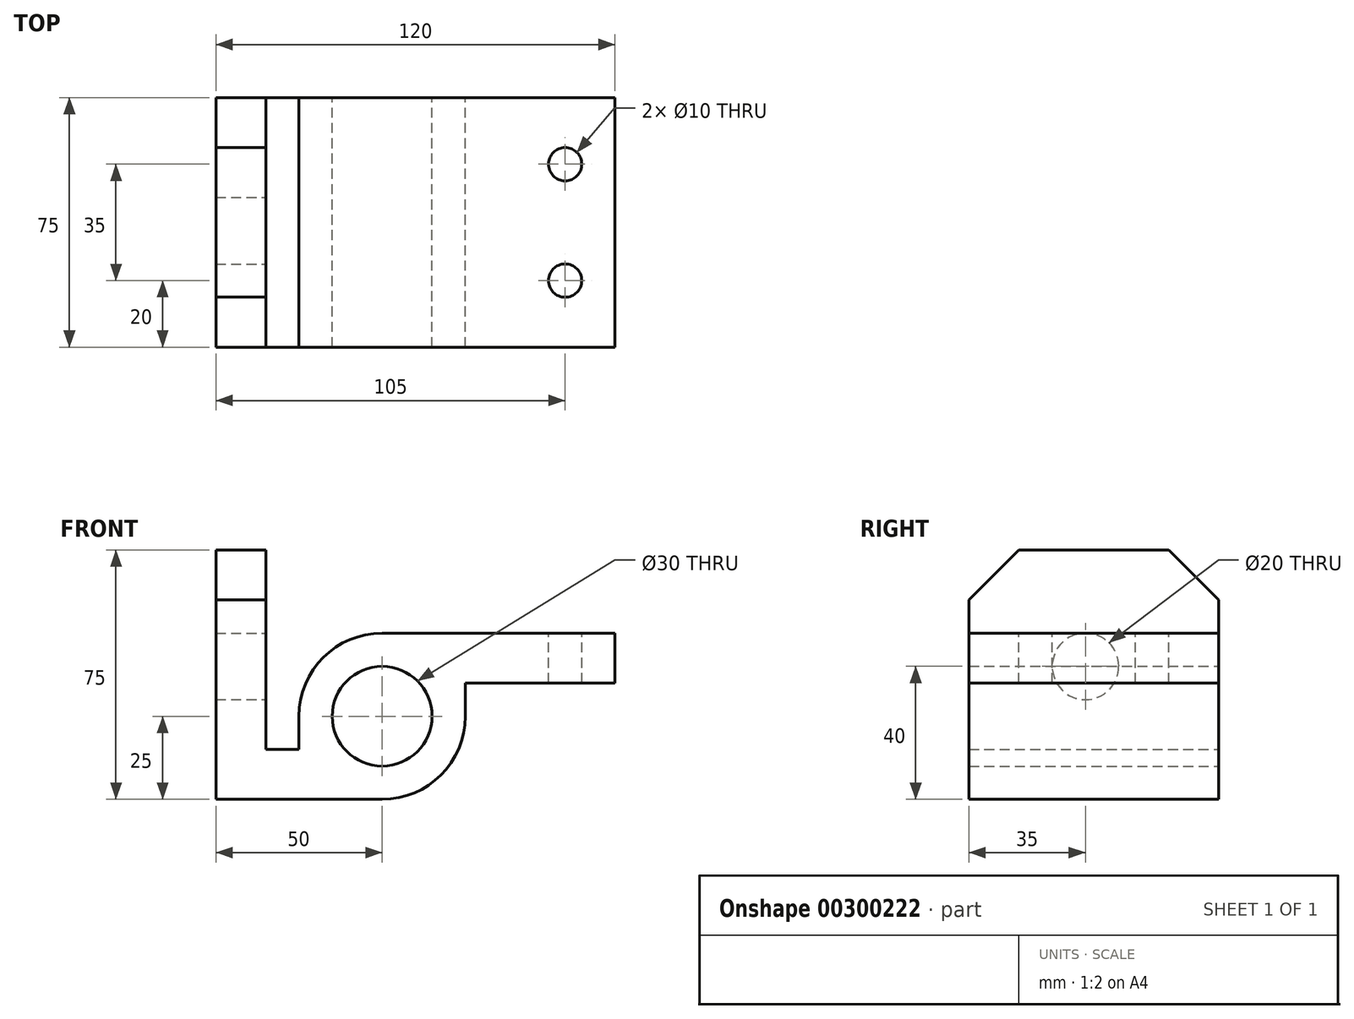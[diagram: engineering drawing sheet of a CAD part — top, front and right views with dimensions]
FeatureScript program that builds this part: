
annotation { "Feature Type Name" : "Feature", "Feature Type Description" : "" }
export const myFeature = defineFeature(function(context is Context, id is Id, definition is map)
    precondition{}
    {
        {
            var Q0;
            Q0=qCreatedBy(makeId("Front.planeOp"),FACE);
            var sketch = newSketch(context, id + "F0", { "sketchPlane" : qUnion([Q0])});
            skLineSegment(sketch, "E0.bottom", {"start": v(0, -25) * mm, "end": v(-25, -25) * mm});
            skLineSegment(sketch, "E0.top", {"start": v(25, 25) * mm, "end": v(0, 25) * mm});
            skLineSegment(sketch, "E0.left", {"start": v(25, 0) * mm, "end": v(25, 25) * mm});
            skLineSegment(sketch, "E0.right", {"start": v(-25, -25) * mm, "end": v(-25, 0) * mm});
            skPoint(sketch, "E0.middle", {"position": v(0, 0) * mm});
            skLineSegment(sketch, "E1", {"start": v(-25, -25) * mm, "end": v(-50, -25) * mm});
            skLineSegment(sketch, "E2", {"start": v(-25, -10) * mm, "end": v(-35, -10) * mm});
            skLineSegment(sketch, "E3", {"start": v(-35, -10) * mm, "end": v(-35, 50) * mm});
            skLineSegment(sketch, "E4", {"start": v(-35, 50) * mm, "end": v(-50, 50) * mm});
            skLineSegment(sketch, "E5", {"start": v(-50, 50) * mm, "end": v(-50, -25) * mm});
            skLineSegment(sketch, "E6", {"start": v(-50, 35) * mm, "end": v(-35, 35) * mm});
            skLineSegment(sketch, "E7", {"start": v(25, 25) * mm, "end": v(70, 25) * mm});
            skLineSegment(sketch, "E8", {"start": v(70, 25) * mm, "end": v(70, 10) * mm});
            skLineSegment(sketch, "E9", {"start": v(70, 10) * mm, "end": v(25, 10) * mm});
            skCircle(sketch, "E10", {"center": v(0, 0) * mm, "radius": 15 * mm});
            skPoint(sketch, "E11.visualSharp", {"position": v(25, -25) * mm});
            skArc(sketch, "E11.filletArc", {"start": v(0, -25) * mm, "mid": v(17.68, -17.68) * mm, "end": v(25, 0) * mm});
            skPoint(sketch, "E12.visualSharp", {"position": v(-25, 25) * mm});
            skArc(sketch, "E12.filletArc", {"start": v(0, 25) * mm, "mid": v(-17.68, 17.68) * mm, "end": v(-25, 0) * mm});
            skSolve(sketch);
        }
        {
            var Q0;
            Q0 = qSketchRegion(id + "F0", true);
            extrude(context, id + "F1", {"entities" : qUnion([Q0]), "endBound" : BoundingType.SYMMETRIC, "depth" : 75 * mm});
        }
        {
            var Q0;
            Q0=makeQuery(id+"F1.opExtrude","CAP_EDGE",EDGE,{"disambiguationData":[OSD([sQuery(id+"F0.wireOp",EDGE,"E4")])],"isStart":false});
            var Q1;
            Q1=makeQuery(id+"F1.opExtrude","CAP_EDGE",EDGE,{"disambiguationData":[OSD([sQuery(id+"F0.wireOp",EDGE,"E4")])],"isStart":true});
            chamfer(context, id + "F2", {"entities" : qUnion([Q0, Q1]), "width" : 15 * mm, "tangentPropagation" : true});
        }
        {
            var Q0;
            Q0=makeQuery(id+"F1.opExtrude","SWEPT_FACE",FACE,{"disambiguationData":[OSD([sQuery(id+"F0.wireOp",EDGE,"E3")])]});
            var sketch = newSketch(context, id + "F3", { "sketchPlane" : qUnion([Q0])});
            skPoint(sketch, "E13.endSnap0", {"position": v(-37.5, 12.5) * mm});
            skCircle(sketch, "E14", {"center": v(-2.5, 15) * mm, "radius": 10 * mm});
            skLineSegment(sketch, "E15", {"start": v(-2.5, 15) * mm, "end": v(-37.5, 15) * mm});
            skLineSegment(sketch, "E16", {"start": v(-2.5, 15) * mm, "end": v(-2.5, 50) * mm});
            skSolve(sketch);
        }
        {
            var Q0;
            {var subQ0=sQuery(id+"F3.wireOp",EDGE,"E15");var subQ1=sQuery(id+"F3.wireOp",EDGE,"E14");var subQ2=makeQuery(id+"F3.imprint","INTERSECT",VERTEX,{"derivedFrom":[subQ1,subQ0]});Q0=makeQuery(id+"F3.imprint","IMPRINT",FACE,{"disambiguationData":[TD([[makeQuery(id+"F3.imprint","IMPRINT",EDGE,{"disambiguationData":[TD([[subQ2,-1.0]])],"derivedFrom":subQ1}),1.0]])]});}
            var Q1;
            Q1=sQuery(id+"F3.wireOp",EDGE,"E14");
            var Q2;
            Q2=makeQuery(id+"F1.opExtrude","SWEPT_FACE",FACE,{"disambiguationData":[OSD([sQuery(id+"F0.wireOp",EDGE,"E5")])]});
            extrude(context, id + "F4", {"entities" : qUnion([Q0]), "operationType" : NewBodyOperationType.ADD, "surfaceEntities" : qUnion([Q1]), "endBound" : BoundingType.UP_TO_SURFACE, "oppositeDirection" : true, "endBoundEntityFace" : qUnion([Q2]), "depth" : 25 * mm});
        }
        {
            var Q0;
            Q0=sQuery(id+"F3.wireOp",VERTEX,"E15.start");
            var Q1;
            Q1=makeQuery(id+"F1.opExtrude","SWEPT_BODY",BODY,{"disambiguationData":[OSD([sQuery(id+"F0.wireOp",EDGE,"E0.bottom"),sQuery(id+"F0.wireOp",EDGE,"E0.top"),sQuery(id+"F0.wireOp",EDGE,"E0.left"),sQuery(id+"F0.wireOp",EDGE,"E0.right"),sQuery(id+"F0.wireOp",EDGE,"E1"),sQuery(id+"F0.wireOp",EDGE,"E2"),sQuery(id+"F0.wireOp",EDGE,"E3"),sQuery(id+"F0.wireOp",EDGE,"E4"),sQuery(id+"F0.wireOp",EDGE,"E5"),sQuery(id+"F0.wireOp",EDGE,"E7"),sQuery(id+"F0.wireOp",EDGE,"E8"),sQuery(id+"F0.wireOp",EDGE,"E9"),sQuery(id+"F0.wireOp",EDGE,"E10"),sQuery(id+"F0.wireOp",EDGE,"E11.filletArc"),sQuery(id+"F0.wireOp",EDGE,"E12.filletArc")])]});
            hole(context, id + "F5", {"style" : HoleStyle.SIMPLE, "endStyle" : HoleEndStyle.THROUGH, "holeDiameter" : 20 * mm, "tappedDepth" : 12 * mm, "tapClearance" : 3, "locations" : qUnion([Q0]), "scope" : qUnion([Q1])});
        }
        {
            var Q0;
            Q0=makeQuery(id+"F1.opExtrude","SWEPT_FACE",FACE,{"disambiguationData":[OSD([sQuery(id+"F0.wireOp",EDGE,"E0.top"),sQuery(id+"F0.wireOp",EDGE,"E7")])]});
            var sketch = newSketch(context, id + "F6", { "sketchPlane" : qUnion([Q0])});
            skCircle(sketch, "E17", {"center": v(55, -17.5) * mm, "radius": 5 * mm});
            skCircle(sketch, "E18", {"center": v(55, 17.5) * mm, "radius": 5 * mm});
            skSolve(sketch);
        }
        {
            var Q0;
            Q0=sQuery(id+"F6.wireOp",VERTEX,"E17.center");
            var Q1;
            Q1=sQuery(id+"F6.wireOp",VERTEX,"E18.center");
            var Q2;
            Q2=makeQuery(id+"F1.opExtrude","SWEPT_BODY",BODY,{"disambiguationData":[OSD([sQuery(id+"F0.wireOp",EDGE,"E0.bottom"),sQuery(id+"F0.wireOp",EDGE,"E0.top"),sQuery(id+"F0.wireOp",EDGE,"E0.left"),sQuery(id+"F0.wireOp",EDGE,"E0.right"),sQuery(id+"F0.wireOp",EDGE,"E1"),sQuery(id+"F0.wireOp",EDGE,"E2"),sQuery(id+"F0.wireOp",EDGE,"E3"),sQuery(id+"F0.wireOp",EDGE,"E4"),sQuery(id+"F0.wireOp",EDGE,"E5"),sQuery(id+"F0.wireOp",EDGE,"E7"),sQuery(id+"F0.wireOp",EDGE,"E8"),sQuery(id+"F0.wireOp",EDGE,"E9"),sQuery(id+"F0.wireOp",EDGE,"E10"),sQuery(id+"F0.wireOp",EDGE,"E11.filletArc"),sQuery(id+"F0.wireOp",EDGE,"E12.filletArc")])]});
            hole(context, id + "F7", {"style" : HoleStyle.SIMPLE, "endStyle" : HoleEndStyle.THROUGH, "holeDiameter" : 10 * mm, "tappedDepth" : 12 * mm, "tapClearance" : 3, "locations" : qUnion([Q0, Q1]), "scope" : qUnion([Q2])});
        }
    });
